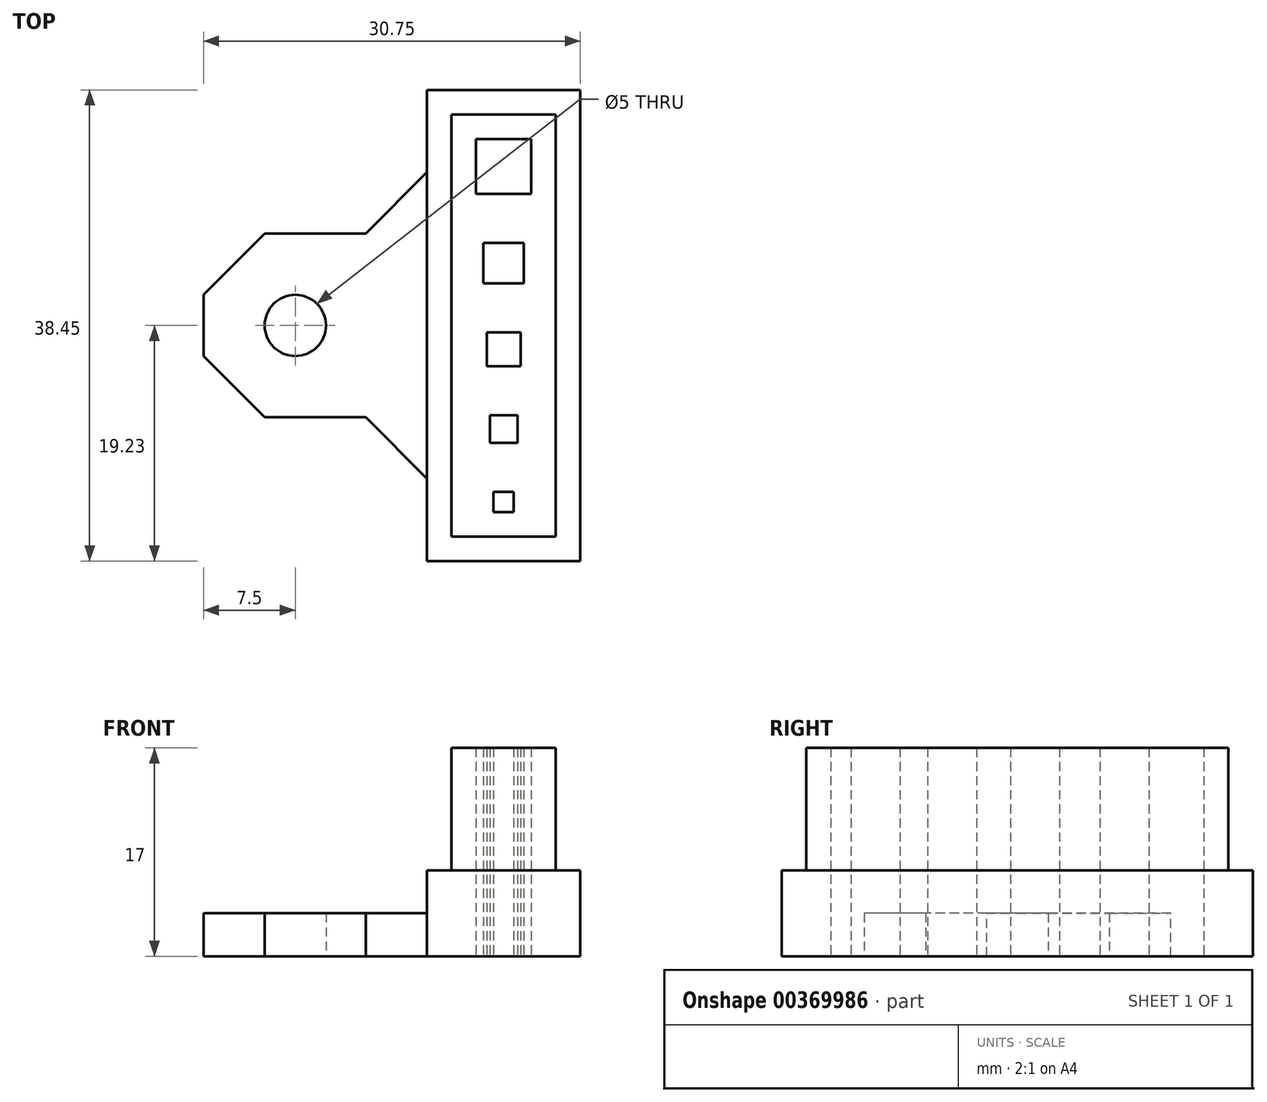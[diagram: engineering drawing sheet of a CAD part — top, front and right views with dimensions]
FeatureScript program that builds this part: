
annotation { "Feature Type Name" : "Feature", "Feature Type Description" : "" }
export const myFeature = defineFeature(function(context is Context, id is Id, definition is map)
    precondition{}
    {
        {
            var Q0;
            Q0=qCreatedBy(makeId("Top.planeOp"),FACE);
            var sketch = newSketch(context, id + "F0", { "sketchPlane" : qUnion([Q0])});
            skLineSegment(sketch, "E0.bottom", {"start": v(0, 19.22) * mm, "end": v(12.5, 19.22) * mm});
            skLineSegment(sketch, "E0.top", {"start": v(0, -19.22) * mm, "end": v(12.5, -19.22) * mm});
            skLineSegment(sketch, "E0.left", {"start": v(0, 19.22) * mm, "end": v(0, 7.5) * mm});
            skLineSegment(sketch, "E0.right", {"start": v(12.5, 19.22) * mm, "end": v(12.5, -19.22) * mm});
            skLineSegment(sketch, "E1.bottom", {"start": v(0, 7.5) * mm, "end": v(-18.25, 7.5) * mm});
            skLineSegment(sketch, "E1.top", {"start": v(0, -7.5) * mm, "end": v(-18.25, -7.5) * mm});
            skLineSegment(sketch, "E1.right", {"start": v(-18.25, 7.5) * mm, "end": v(-18.25, -7.5) * mm});
            skCircle(sketch, "E2", {"center": v(-10.75, 0) * mm, "radius": 2.5 * mm});
            skLineSegment(sketch, "E3.trimOffspring", {"start": v(0, -7.5) * mm, "end": v(0, -19.22) * mm});
            skLineSegment(sketch, "E4", {"start": v(6.25, 19.22) * mm, "end": v(6.25, -19.22) * mm, "construction": true});
            skLineSegment(sketch, "E5.bottom", {"start": v(8.5, 10.72) * mm, "end": v(4, 10.72) * mm});
            skLineSegment(sketch, "E5.top", {"start": v(8.5, 15.23) * mm, "end": v(4, 15.23) * mm});
            skLineSegment(sketch, "E5.left", {"start": v(8.5, 10.72) * mm, "end": v(8.5, 15.23) * mm});
            skLineSegment(sketch, "E5.right", {"start": v(4, 10.72) * mm, "end": v(4, 15.23) * mm});
            skPoint(sketch, "E5.middle", {"position": v(6.25, 12.97) * mm});
            skLineSegment(sketch, "E6.bottom", {"start": v(7.9, 3.42) * mm, "end": v(4.6, 3.42) * mm});
            skLineSegment(sketch, "E6.top", {"start": v(7.9, 6.72) * mm, "end": v(4.6, 6.72) * mm});
            skLineSegment(sketch, "E6.left", {"start": v(7.9, 3.42) * mm, "end": v(7.9, 6.72) * mm});
            skLineSegment(sketch, "E6.right", {"start": v(4.6, 3.42) * mm, "end": v(4.6, 6.72) * mm});
            skPoint(sketch, "E6.middle", {"position": v(6.25, 5.07) * mm});
            skLineSegment(sketch, "E7.bottom", {"start": v(7.63, -3.32) * mm, "end": v(4.88, -3.32) * mm});
            skLineSegment(sketch, "E7.top", {"start": v(7.63, -0.57) * mm, "end": v(4.88, -0.57) * mm});
            skLineSegment(sketch, "E7.left", {"start": v(7.63, -3.32) * mm, "end": v(7.63, -0.57) * mm});
            skLineSegment(sketch, "E7.right", {"start": v(4.88, -3.32) * mm, "end": v(4.88, -0.57) * mm});
            skPoint(sketch, "E7.middle", {"position": v(6.25, -1.95) * mm});
            skLineSegment(sketch, "E8.bottom", {"start": v(7.38, -9.57) * mm, "end": v(5.13, -9.57) * mm});
            skLineSegment(sketch, "E8.top", {"start": v(7.38, -7.33) * mm, "end": v(5.13, -7.33) * mm});
            skLineSegment(sketch, "E8.left", {"start": v(7.38, -9.57) * mm, "end": v(7.38, -7.33) * mm});
            skLineSegment(sketch, "E8.right", {"start": v(5.13, -9.57) * mm, "end": v(5.13, -7.33) * mm});
            skPoint(sketch, "E8.middle", {"position": v(6.25, -8.45) * mm});
            skLineSegment(sketch, "E9.bottom", {"start": v(7.08, -15.23) * mm, "end": v(5.43, -15.23) * mm});
            skLineSegment(sketch, "E9.top", {"start": v(7.08, -13.58) * mm, "end": v(5.43, -13.58) * mm});
            skLineSegment(sketch, "E9.left", {"start": v(7.08, -15.23) * mm, "end": v(7.08, -13.58) * mm});
            skLineSegment(sketch, "E9.right", {"start": v(5.43, -15.23) * mm, "end": v(5.43, -13.58) * mm});
            skPoint(sketch, "E9.middle", {"position": v(6.25, -14.4) * mm});
            skSolve(sketch);
        }
        {
            var Q0;
            Q0 = qSketchRegion(id + "F0", true);
            extrude(context, id + "F1", {"entities" : qUnion([Q0]), "depth" : 3.5 * mm});
        }
        {
            var Q0;
            Q0=makeQuery(id+"F1.opExtrude","CAP_FACE",FACE,{"disambiguationData":[OSD([sQuery(id+"F0.wireOp",EDGE,"E0.bottom"),sQuery(id+"F0.wireOp",EDGE,"E0.top"),sQuery(id+"F0.wireOp",EDGE,"E0.left"),sQuery(id+"F0.wireOp",EDGE,"E0.right"),sQuery(id+"F0.wireOp",EDGE,"E1.bottom"),sQuery(id+"F0.wireOp",EDGE,"E1.top"),sQuery(id+"F0.wireOp",EDGE,"E1.right"),sQuery(id+"F0.wireOp",EDGE,"E2"),sQuery(id+"F0.wireOp",EDGE,"E3.trimOffspring"),sQuery(id+"F0.wireOp",EDGE,"E5.bottom"),sQuery(id+"F0.wireOp",EDGE,"E5.top"),sQuery(id+"F0.wireOp",EDGE,"E5.left"),sQuery(id+"F0.wireOp",EDGE,"E5.right"),sQuery(id+"F0.wireOp",EDGE,"E6.bottom"),sQuery(id+"F0.wireOp",EDGE,"E6.top"),sQuery(id+"F0.wireOp",EDGE,"E6.left"),sQuery(id+"F0.wireOp",EDGE,"E6.right"),sQuery(id+"F0.wireOp",EDGE,"E7.bottom"),sQuery(id+"F0.wireOp",EDGE,"E7.top"),sQuery(id+"F0.wireOp",EDGE,"E7.left"),sQuery(id+"F0.wireOp",EDGE,"E7.right"),sQuery(id+"F0.wireOp",EDGE,"E8.bottom"),sQuery(id+"F0.wireOp",EDGE,"E8.top"),sQuery(id+"F0.wireOp",EDGE,"E8.left"),sQuery(id+"F0.wireOp",EDGE,"E8.right"),sQuery(id+"F0.wireOp",EDGE,"E9.bottom"),sQuery(id+"F0.wireOp",EDGE,"E9.top"),sQuery(id+"F0.wireOp",EDGE,"E9.left"),sQuery(id+"F0.wireOp",EDGE,"E9.right")])],"isStart":false});
            var sketch = newSketch(context, id + "F2", { "sketchPlane" : qUnion([Q0])});
            skLineSegment(sketch, "E10.0", {"start": v(0, 19.22) * mm, "end": v(12.5, 19.22) * mm});
            skLineSegment(sketch, "E11.0", {"start": v(12.5, 19.22) * mm, "end": v(12.5, -19.22) * mm});
            skLineSegment(sketch, "E12.0", {"start": v(0, -19.22) * mm, "end": v(12.5, -19.22) * mm});
            skLineSegment(sketch, "E13", {"start": v(0, 19.22) * mm, "end": v(0, -19.22) * mm});
            skSolve(sketch);
        }
        {
            var Q0;
            {var subQ1=sQuery(id+"F2.wireOp",EDGE,"E10.0");Q0=makeQuery(id+"F2.imprint","IMPRINT",FACE,{"disambiguationData":[TD([[makeQuery(id+"F2.imprint","IMPRINT",EDGE,{"derivedFrom":subQ1}),-1.0]])]});}
            extrude(context, id + "F3", {"entities" : qUnion([Q0]), "operationType" : NewBodyOperationType.ADD, "depth" : 3.5 * mm});
        }
        {
            var Q0;
            Q0=makeQuery(id+"F3.opExtrude","CAP_FACE",FACE,{"disambiguationData":[OSD([sQuery(id+"F0.wireOp",EDGE,"E5.bottom"),sQuery(id+"F0.wireOp",EDGE,"E5.top"),sQuery(id+"F0.wireOp",EDGE,"E5.left"),sQuery(id+"F0.wireOp",EDGE,"E5.right"),sQuery(id+"F0.wireOp",EDGE,"E6.bottom"),sQuery(id+"F0.wireOp",EDGE,"E6.top"),sQuery(id+"F0.wireOp",EDGE,"E6.left"),sQuery(id+"F0.wireOp",EDGE,"E6.right"),sQuery(id+"F0.wireOp",EDGE,"E7.bottom"),sQuery(id+"F0.wireOp",EDGE,"E7.top"),sQuery(id+"F0.wireOp",EDGE,"E7.left"),sQuery(id+"F0.wireOp",EDGE,"E7.right"),sQuery(id+"F0.wireOp",EDGE,"E8.bottom"),sQuery(id+"F0.wireOp",EDGE,"E8.top"),sQuery(id+"F0.wireOp",EDGE,"E8.left"),sQuery(id+"F0.wireOp",EDGE,"E8.right"),sQuery(id+"F0.wireOp",EDGE,"E9.bottom"),sQuery(id+"F0.wireOp",EDGE,"E9.top"),sQuery(id+"F0.wireOp",EDGE,"E9.left"),sQuery(id+"F0.wireOp",EDGE,"E9.right"),sQuery(id+"F2.wireOp",EDGE,"E10.0"),sQuery(id+"F2.wireOp",EDGE,"E11.0"),sQuery(id+"F2.wireOp",EDGE,"E12.0"),sQuery(id+"F2.wireOp",EDGE,"E13")])],"isStart":false});
            var sketch = newSketch(context, id + "F4", { "sketchPlane" : qUnion([Q0])});
            skLineSegment(sketch, "E14", {"start": v(7.5, 6.72) * mm, "end": v(4.5, 6.72) * mm});
            skLineSegment(sketch, "E15", {"start": v(7.9, 3.5) * mm, "end": v(7.9, 6.5) * mm});
            skLineSegment(sketch, "E16", {"start": v(7.5, 3.42) * mm, "end": v(4.5, 3.42) * mm});
            skLineSegment(sketch, "E17", {"start": v(4.6, 3.5) * mm, "end": v(4.6, 6.5) * mm});
            skLineSegment(sketch, "E18", {"start": v(7.25, -0.57) * mm, "end": v(4.75, -0.57) * mm});
            skLineSegment(sketch, "E19", {"start": v(7.63, -3) * mm, "end": v(7.63, -0.5) * mm});
            skLineSegment(sketch, "E20", {"start": v(7.25, -3.32) * mm, "end": v(4.75, -3.32) * mm});
            skLineSegment(sketch, "E21", {"start": v(4.88, -3) * mm, "end": v(4.88, -0.5) * mm});
            skLineSegment(sketch, "E22", {"start": v(7, -7.33) * mm, "end": v(5, -7.33) * mm});
            skLineSegment(sketch, "E23", {"start": v(7.38, -9) * mm, "end": v(7.38, -7) * mm});
            skLineSegment(sketch, "E24", {"start": v(7, -9.57) * mm, "end": v(5, -9.57) * mm});
            skLineSegment(sketch, "E25", {"start": v(5.13, -9) * mm, "end": v(5.13, -7) * mm});
            skLineSegment(sketch, "E26", {"start": v(6.75, -13.58) * mm, "end": v(5.25, -13.58) * mm});
            skLineSegment(sketch, "E27", {"start": v(7.08, -14.5) * mm, "end": v(7.08, -13) * mm});
            skLineSegment(sketch, "E28", {"start": v(6.75, -15.23) * mm, "end": v(5.25, -15.23) * mm});
            skLineSegment(sketch, "E29", {"start": v(5.43, -14.5) * mm, "end": v(5.43, -13) * mm});
            skLineSegment(sketch, "E30", {"start": v(0, 18.5) * mm, "end": v(0, -18.5) * mm});
            skLineSegment(sketch, "E31", {"start": v(0, 19.22) * mm, "end": v(12, 19.22) * mm});
            skLineSegment(sketch, "E32", {"start": v(12.5, 18.5) * mm, "end": v(12.5, -18.5) * mm});
            skLineSegment(sketch, "E33", {"start": v(0, -19.22) * mm, "end": v(12, -19.22) * mm});
            skLineSegment(sketch, "E34", {"start": v(4, 10.5) * mm, "end": v(4, 14.5) * mm});
            skLineSegment(sketch, "E35", {"start": v(8, 10.72) * mm, "end": v(4, 10.72) * mm});
            skLineSegment(sketch, "E36", {"start": v(8.5, 10.5) * mm, "end": v(8.5, 14.5) * mm});
            skLineSegment(sketch, "E37", {"start": v(8, 15.23) * mm, "end": v(4, 15.23) * mm});
            skLineSegment(sketch, "E38.0", {"start": v(2, 17.22) * mm, "end": v(10.5, 17.22) * mm});
            skLineSegment(sketch, "E38.1", {"start": v(2, 17.22) * mm, "end": v(2, -17.22) * mm});
            skLineSegment(sketch, "E38.2", {"start": v(2, -17.22) * mm, "end": v(10.5, -17.22) * mm});
            skLineSegment(sketch, "E38.3", {"start": v(10.5, 17.22) * mm, "end": v(10.5, -17.22) * mm});
            skSolve(sketch);
        }
        {
            var Q0;
            Q0=makeQuery(id+"F4.imprint","IMPRINT",FACE,{"disambiguationData":[TD([[makeQuery(id+"F4.imprint","IMPRINT",EDGE,{"derivedFrom":sQuery(id+"F4.wireOp",EDGE,"E14")}),-1.0]])]});
            extrude(context, id + "F5", {"entities" : qUnion([Q0]), "operationType" : NewBodyOperationType.ADD, "depth" : 10 * mm});
        }
        {
            var Q0;
            Q0=makeQuery(id+"F1.opExtrude","SWEPT_EDGE",EDGE,{"disambiguationData":[OSD([sQuery(id+"F0.wireOp",EDGE,"E0.left"),sQuery(id+"F0.wireOp",EDGE,"E1.bottom")])]});
            var Q1;
            Q1=makeQuery(id+"F1.opExtrude","SWEPT_EDGE",EDGE,{"disambiguationData":[OSD([sQuery(id+"F0.wireOp",EDGE,"E1.top"),sQuery(id+"F0.wireOp",EDGE,"E3.trimOffspring")])]});
            var Q2;
            Q2=makeQuery(id+"F1.opExtrude","SWEPT_EDGE",EDGE,{"disambiguationData":[OSD([sQuery(id+"F0.wireOp",EDGE,"E1.top"),sQuery(id+"F0.wireOp",EDGE,"E1.right")])]});
            var Q3;
            Q3=makeQuery(id+"F1.opExtrude","SWEPT_EDGE",EDGE,{"disambiguationData":[OSD([sQuery(id+"F0.wireOp",EDGE,"E1.bottom"),sQuery(id+"F0.wireOp",EDGE,"E1.right")])]});
            chamfer(context, id + "F6", {"entities" : qUnion([Q0, Q1, Q2, Q3]), "width" : 5 * mm, "tangentPropagation" : true});
        }
    });
